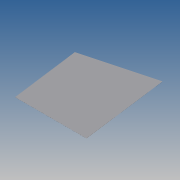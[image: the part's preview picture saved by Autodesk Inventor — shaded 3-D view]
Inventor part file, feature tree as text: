
AUTODESK INVENTOR PART (.ipt)
format: ipt  version: 2014 SP1 (Build 180222100, 222)  size: 71,680 bytes
history: native  units: in
note: dims shown in document units (in); Inventor stores cm internally (conversion verified against a paired STEP export)
features: extrude x1, sketch x1
ambient origin geometry x8: Origin, YZ Plane, XZ Plane, XY Plane, X Axis, Y Axis, Z Axis, Center Point
bodies: Solid1 (feature_tree)
feature tree (2):
  extrude  "Extrusion1"  Depth=0.0394in
  sketch  "Sketch1"  dims[d0=165.0deg d3=1.9685in d4=1.9685in d6=163.3858in d7=1.1853in d8=0.0394in d9=0.0in]
